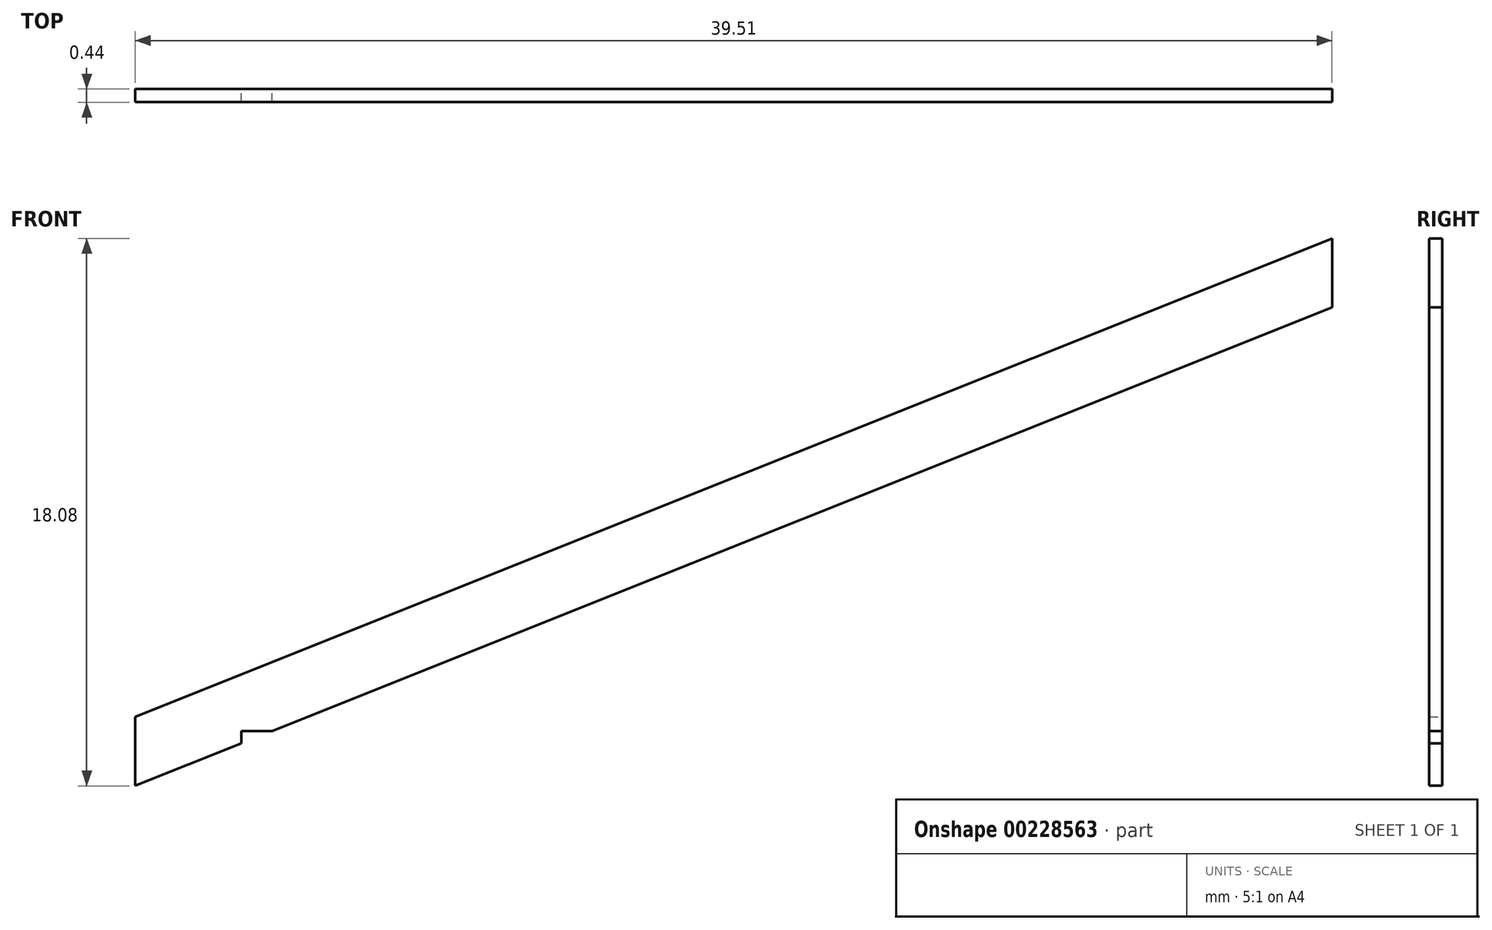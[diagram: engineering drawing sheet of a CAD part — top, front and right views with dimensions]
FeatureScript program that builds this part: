
annotation { "Feature Type Name" : "Feature", "Feature Type Description" : "" }
export const myFeature = defineFeature(function(context is Context, id is Id, definition is map)
    precondition{}
    {
        {
            var Q0;
            Q0=qCreatedBy(makeId("Front.planeOp"),FACE);
            var sketch = newSketch(context, id + "F0", { "sketchPlane" : qUnion([Q0])});
            skLineSegment(sketch, "E0", {"start": v(0, 0) * mm, "end": v(0, 2863.85) * mm, "construction": true});
            skLineSegment(sketch, "E1", {"start": v(0, 2863.85) * mm, "end": v(3048, 4083.05) * mm, "construction": true});
            skLineSegment(sketch, "E2", {"start": v(3048, 4083.05) * mm, "end": v(3048, 0) * mm, "construction": true});
            skLineSegment(sketch, "E3", {"start": v(3048, 0) * mm, "end": v(0, 0) * mm, "construction": true});
            skLineSegment(sketch, "E4", {"start": v(0, 2863.85) * mm, "end": v(-88.9, 2863.85) * mm, "construction": true});
            skLineSegment(sketch, "E5", {"start": v(-88.9, 2863.85) * mm, "end": v(-88.9, 0) * mm, "construction": true});
            skLineSegment(sketch, "E6", {"start": v(-88.9, 0) * mm, "end": v(0, 0) * mm, "construction": true});
            skSolve(sketch);
        }
        {
            var Q0;
            Q0=qCreatedBy(makeId("Front.planeOp"),FACE);
            var sketch = newSketch(context, id + "F1", { "sketchPlane" : qUnion([Q0])});
            skLineSegment(sketch, "E7", {"start": v(3048, 4083.05) * mm, "end": v(0, 2863.85) * mm});
            skLineSegment(sketch, "E8", {"start": v(3048, 4083.05) * mm, "end": v(3048, 4281.39) * mm});
            skLineSegment(sketch, "E9", {"start": v(3048, 4281.39) * mm, "end": v(-393.7, 2904.7) * mm});
            skLineSegment(sketch, "E10", {"start": v(-393.7, 2706.37) * mm, "end": v(-88.9, 2828.29) * mm});
            skLineSegment(sketch, "E11", {"start": v(0, 2863.85) * mm, "end": v(-88.9, 2863.85) * mm});
            skLineSegment(sketch, "E12", {"start": v(-88.9, 2863.85) * mm, "end": v(-88.9, 2828.29) * mm});
            skPoint(sketch, "E13.orphan", {"position": v(0, 2863.85) * mm});
            skLineSegment(sketch, "E14", {"start": v(-393.7, 2706.37) * mm, "end": v(-393.7, 2904.7) * mm});
            skSolve(sketch);
        }
        {
            var Q0;
            Q0=makeQuery(id+"F1.imprint","IMPRINT",FACE,{"disambiguationData":[TD([[makeQuery(id+"F1.imprint","IMPRINT",EDGE,{"derivedFrom":sQuery(id+"F1.wireOp",EDGE,"E7")}),-1.0]])]});
            extrude(context, id + "F2", {"entities" : qUnion([Q0]), "depth" : 38.1 * mm});
        }
        {
            var Q0;
            Q0=makeQuery(id+"F2.opExtrude","SWEPT_BODY",BODY,{"disambiguationData":[OSD([sQuery(id+"F1.wireOp",EDGE,"E7"),sQuery(id+"F1.wireOp",EDGE,"E8"),sQuery(id+"F1.wireOp",EDGE,"E9"),sQuery(id+"F1.wireOp",EDGE,"E10"),sQuery(id+"F1.wireOp",EDGE,"E11"),sQuery(id+"F1.wireOp",EDGE,"E12"),sQuery(id+"F1.wireOp",EDGE,"E14")])]});
            var Q1;
            Q1=qCreatedBy(makeId("Origin.pointOp"),VERTEX);
            transform(context, id + "F3", {"entities" : qUnion([Q0]), "transformType" : TransformType.SCALE_UNIFORMLY, "scale" : 1 / 87.1, "scalePoint" : qUnion([Q1]), "makeCopy" : false});
        }
    });
